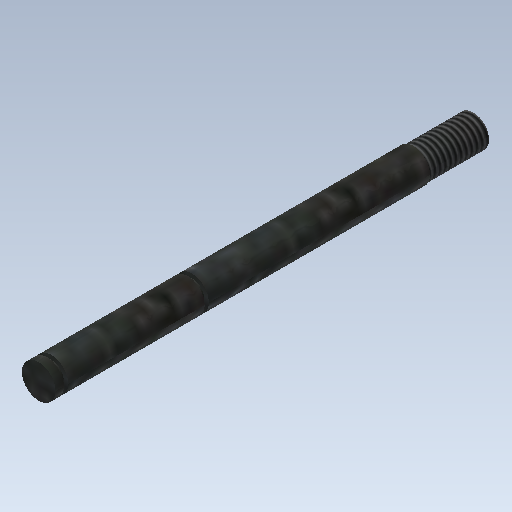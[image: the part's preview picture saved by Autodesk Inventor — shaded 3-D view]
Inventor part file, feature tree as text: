
AUTODESK INVENTOR PART (.ipt)
format: ipt  version: 2020 (Build 240168000, 168)  size: 133,120 bytes
history: native  units: mm
features: revolve x1, thread x1, sketch x1
ambient origin geometry x8: Origin, YZ Plane, XZ Plane, XY Plane, X Axis, Y Axis, Z Axis, Center Point
bodies: Solid1 (feature_tree)
feature tree (3):
  revolve  "Revolution1"  [1 undecoded]
  thread  "Thread1"  [1 undecoded]
  sketch  "Sketch1"  dims[d0=5.7mm d1=21.4mm d2=0.8mm d3=0.4mm d4=1.2mm d5=1.6mm d6=0.4mm d7=1.5mm d8=90.0deg d9=10.0mm d10=0.0mm]
note: 2 required parameter values undecoded (feature->parameter linkage not recoverable at this tier; creation-order binding heuristic only, values carry confidence <= 0.55)